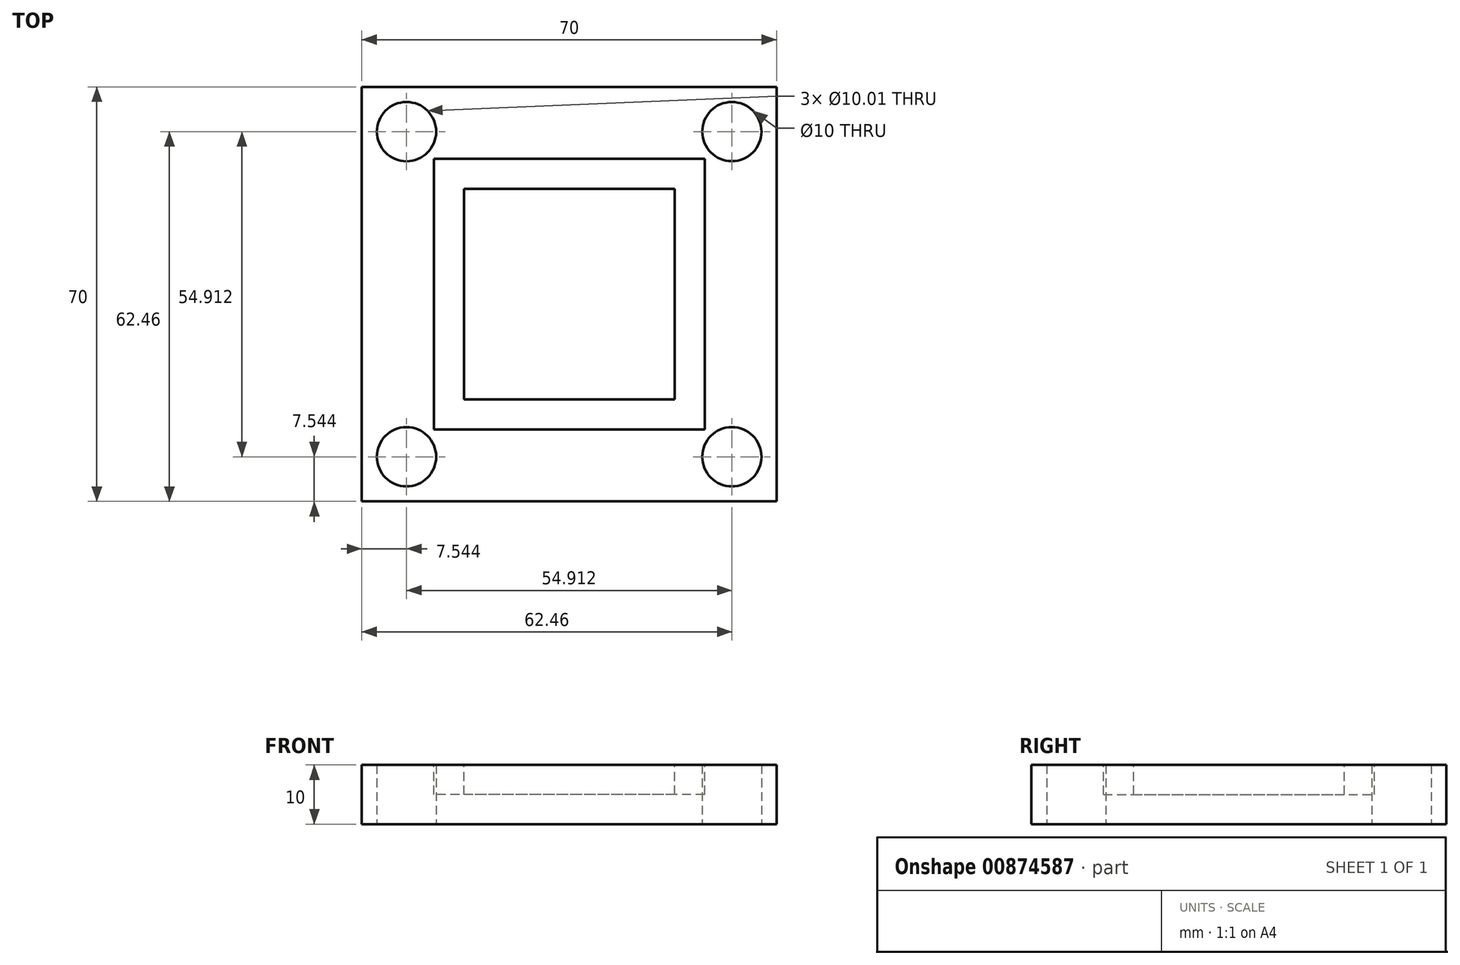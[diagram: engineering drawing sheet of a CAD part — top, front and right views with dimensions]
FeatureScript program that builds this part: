
annotation { "Feature Type Name" : "Feature", "Feature Type Description" : "" }
export const myFeature = defineFeature(function(context is Context, id is Id, definition is map)
    precondition{}
    {
        {
            var Q0;
            Q0=qCreatedBy(makeId("Top.planeOp"),FACE);
            var sketch = newSketch(context, id + "F0", { "sketchPlane" : qUnion([Q0])});
            skLineSegment(sketch, "E0.bottom", {"start": v(-35, 35) * mm, "end": v(35, 35) * mm});
            skLineSegment(sketch, "E0.top", {"start": v(-35, -35) * mm, "end": v(35, -35) * mm});
            skLineSegment(sketch, "E0.left", {"start": v(-35, 35) * mm, "end": v(-35, -35) * mm});
            skLineSegment(sketch, "E0.right", {"start": v(35, 35) * mm, "end": v(35, -35) * mm});
            skPoint(sketch, "E0.middle", {"position": v(0, 0) * mm});
            skCircle(sketch, "E1", {"center": v(27.46, 27.46) * mm, "radius": 5 * mm});
            skCircle(sketch, "E2", {"center": v(27.46, -27.46) * mm, "radius": 5 * mm});
            skCircle(sketch, "E3", {"center": v(-27.46, 27.46) * mm, "radius": 5 * mm});
            skCircle(sketch, "E4", {"center": v(-27.46, -27.46) * mm, "radius": 5 * mm});
            skSolve(sketch);
        }
        {
            var Q0;
            Q0=makeQuery(id+"F0.imprint","IMPRINT",FACE,{"disambiguationData":[TD([[makeQuery(id+"F0.imprint","IMPRINT",EDGE,{"derivedFrom":sQuery(id+"F0.wireOp",EDGE,"E0.bottom")}),-1.0]])]});
            extrude(context, id + "F1", {"entities" : qUnion([Q0]), "depth" : 10 * mm, "offsetDistance" : 25.4 * mm});
        }
        {
            var Q0;
            Q0=makeQuery(id+"F1.opExtrude","CAP_FACE",FACE,{"disambiguationData":[OSD([sQuery(id+"F0.wireOp",EDGE,"E0.bottom"),sQuery(id+"F0.wireOp",EDGE,"E0.top"),sQuery(id+"F0.wireOp",EDGE,"E0.left"),sQuery(id+"F0.wireOp",EDGE,"E0.right"),sQuery(id+"F0.wireOp",EDGE,"E1"),sQuery(id+"F0.wireOp",EDGE,"E2"),sQuery(id+"F0.wireOp",EDGE,"E3"),sQuery(id+"F0.wireOp",EDGE,"E4")])],"isStart":false});
            var sketch = newSketch(context, id + "F2", { "sketchPlane" : qUnion([Q0])});
            skLineSegment(sketch, "E5.bottom", {"start": v(17.78, -17.78) * mm, "end": v(-17.78, -17.78) * mm});
            skLineSegment(sketch, "E5.top", {"start": v(17.78, 17.78) * mm, "end": v(-17.78, 17.78) * mm});
            skLineSegment(sketch, "E5.left", {"start": v(17.78, -17.78) * mm, "end": v(17.78, 17.78) * mm});
            skLineSegment(sketch, "E5.right", {"start": v(-17.78, -17.78) * mm, "end": v(-17.78, 17.78) * mm});
            skPoint(sketch, "E5.middle", {"position": v(0, 0) * mm});
            skLineSegment(sketch, "E6.bottom", {"start": v(22.86, -22.86) * mm, "end": v(-22.86, -22.86) * mm});
            skLineSegment(sketch, "E6.top", {"start": v(22.86, 22.86) * mm, "end": v(-22.86, 22.86) * mm});
            skLineSegment(sketch, "E6.left", {"start": v(22.86, -22.86) * mm, "end": v(22.86, 22.86) * mm});
            skLineSegment(sketch, "E6.right", {"start": v(-22.86, -22.86) * mm, "end": v(-22.86, 22.86) * mm});
            skSolve(sketch);
        }
        {
            var Q0;
            Q0=makeQuery(id+"F2.imprint","IMPRINT",FACE,{"disambiguationData":[TD([[makeQuery(id+"F2.imprint","IMPRINT",EDGE,{"derivedFrom":sQuery(id+"F2.wireOp",EDGE,"E5.bottom")}),1.0]])]});
            extrude(context, id + "F3", {"entities" : qUnion([Q0]), "operationType" : NewBodyOperationType.REMOVE, "oppositeDirection" : true, "depth" : 5 * mm, "offsetDistance" : 25.4 * mm});
        }
    });
